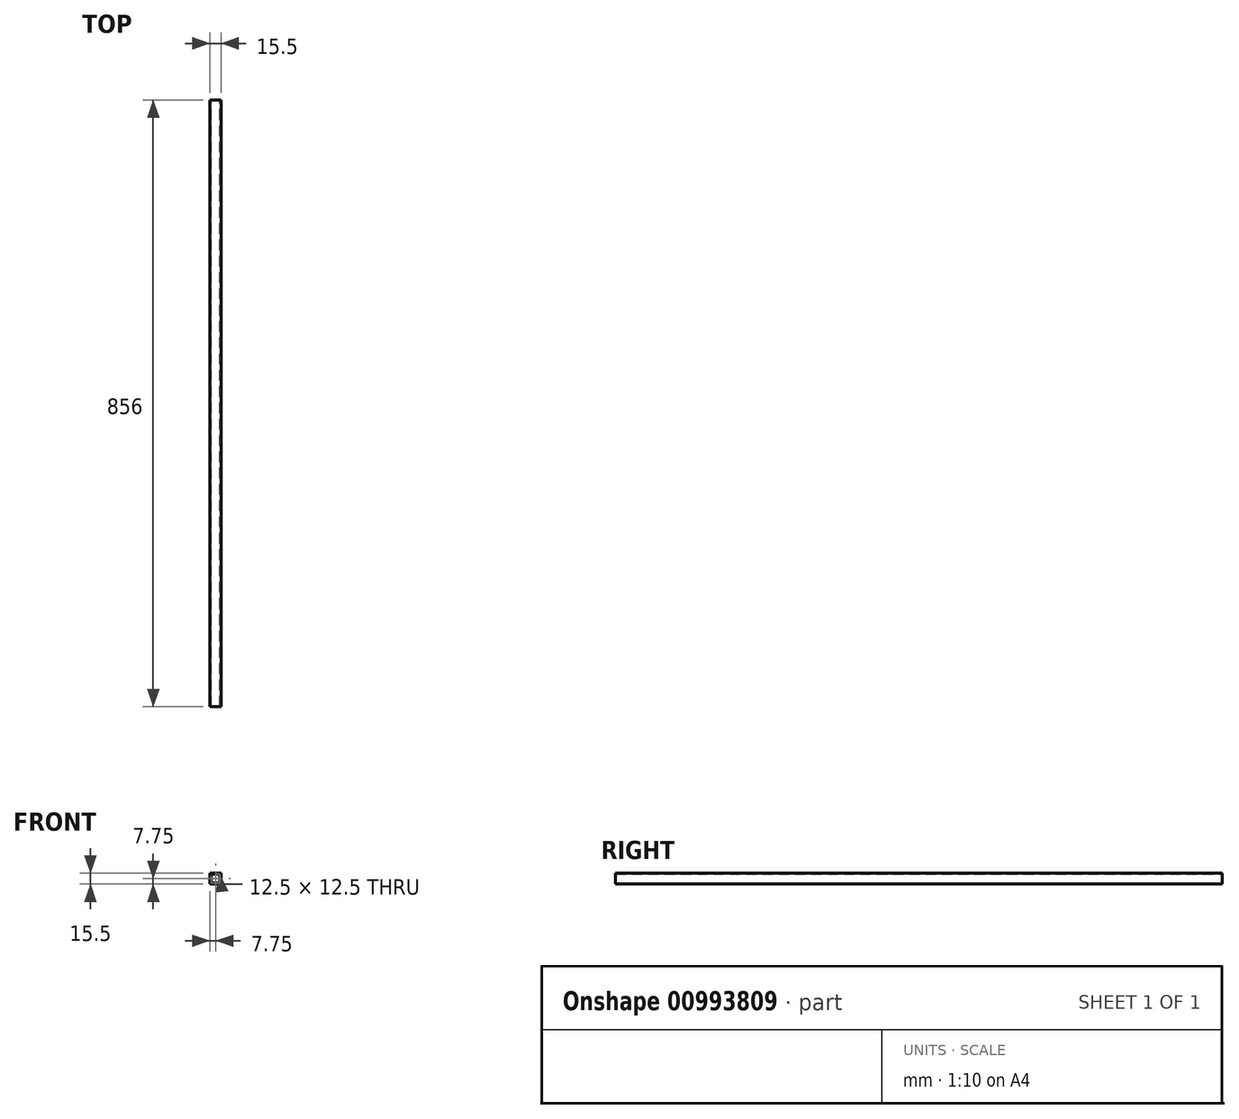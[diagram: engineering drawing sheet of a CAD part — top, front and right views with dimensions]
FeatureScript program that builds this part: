
annotation { "Feature Type Name" : "Feature", "Feature Type Description" : "" }
export const myFeature = defineFeature(function(context is Context, id is Id, definition is map)
    precondition{}
    {
        {
            var Q0;
            Q0=qCreatedBy(makeId("Front.planeOp"),FACE);
            var sketch = newSketch(context, id + "F0", { "sketchPlane" : qUnion([Q0])});
            skLineSegment(sketch, "E0.bottom", {"start": v(7.75, 7.75) * mm, "end": v(-7.75, 7.75) * mm});
            skLineSegment(sketch, "E0.top", {"start": v(7.75, -7.75) * mm, "end": v(-7.75, -7.75) * mm});
            skLineSegment(sketch, "E0.left", {"start": v(7.75, 7.75) * mm, "end": v(7.75, -7.75) * mm});
            skLineSegment(sketch, "E0.right", {"start": v(-7.75, 7.75) * mm, "end": v(-7.75, -7.75) * mm});
            skPoint(sketch, "E0.middle", {"position": v(0, 0) * mm});
            skLineSegment(sketch, "E1.bottom", {"start": v(6.25, 6.25) * mm, "end": v(-6.25, 6.25) * mm});
            skLineSegment(sketch, "E1.top", {"start": v(6.25, -6.25) * mm, "end": v(-6.25, -6.25) * mm});
            skLineSegment(sketch, "E1.left", {"start": v(6.25, 6.25) * mm, "end": v(6.25, -6.25) * mm});
            skLineSegment(sketch, "E1.right", {"start": v(-6.25, 6.25) * mm, "end": v(-6.25, -6.25) * mm});
            skSolve(sketch);
        }
        {
            var Q0;
            Q0=makeQuery(id+"F0.imprint","IMPRINT",FACE,{"disambiguationData":[TD([[makeQuery(id+"F0.imprint","IMPRINT",EDGE,{"derivedFrom":sQuery(id+"F0.wireOp",EDGE,"E0.bottom")}),1.0]])]});
            extrude(context, id + "F1", {"entities" : qUnion([Q0]), "depth" : 856 * mm, "offsetDistance" : 25 * mm, "symmetric" : true});
        }
    });
